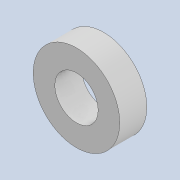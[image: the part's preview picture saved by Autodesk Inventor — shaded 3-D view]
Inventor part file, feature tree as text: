
AUTODESK INVENTOR PART (.ipt)
format: ipt  version: 2020 (Build 240168000, 168)  size: 83,456 bytes
history: native  units: mm
features: extrude x1, sketch x1
ambient origin geometry x8: Origin, YZ Plane, XZ Plane, XY Plane, X Axis, Y Axis, Z Axis, Center Point
bodies: Solid1 (feature_tree)
feature tree (2):
  extrude  "Extrusion1"  Depth=5.0mm
  sketch  "Sketch1"  dims[d0=8.0mm d1=16.0mm d2=5.0mm d3=0.0mm]
